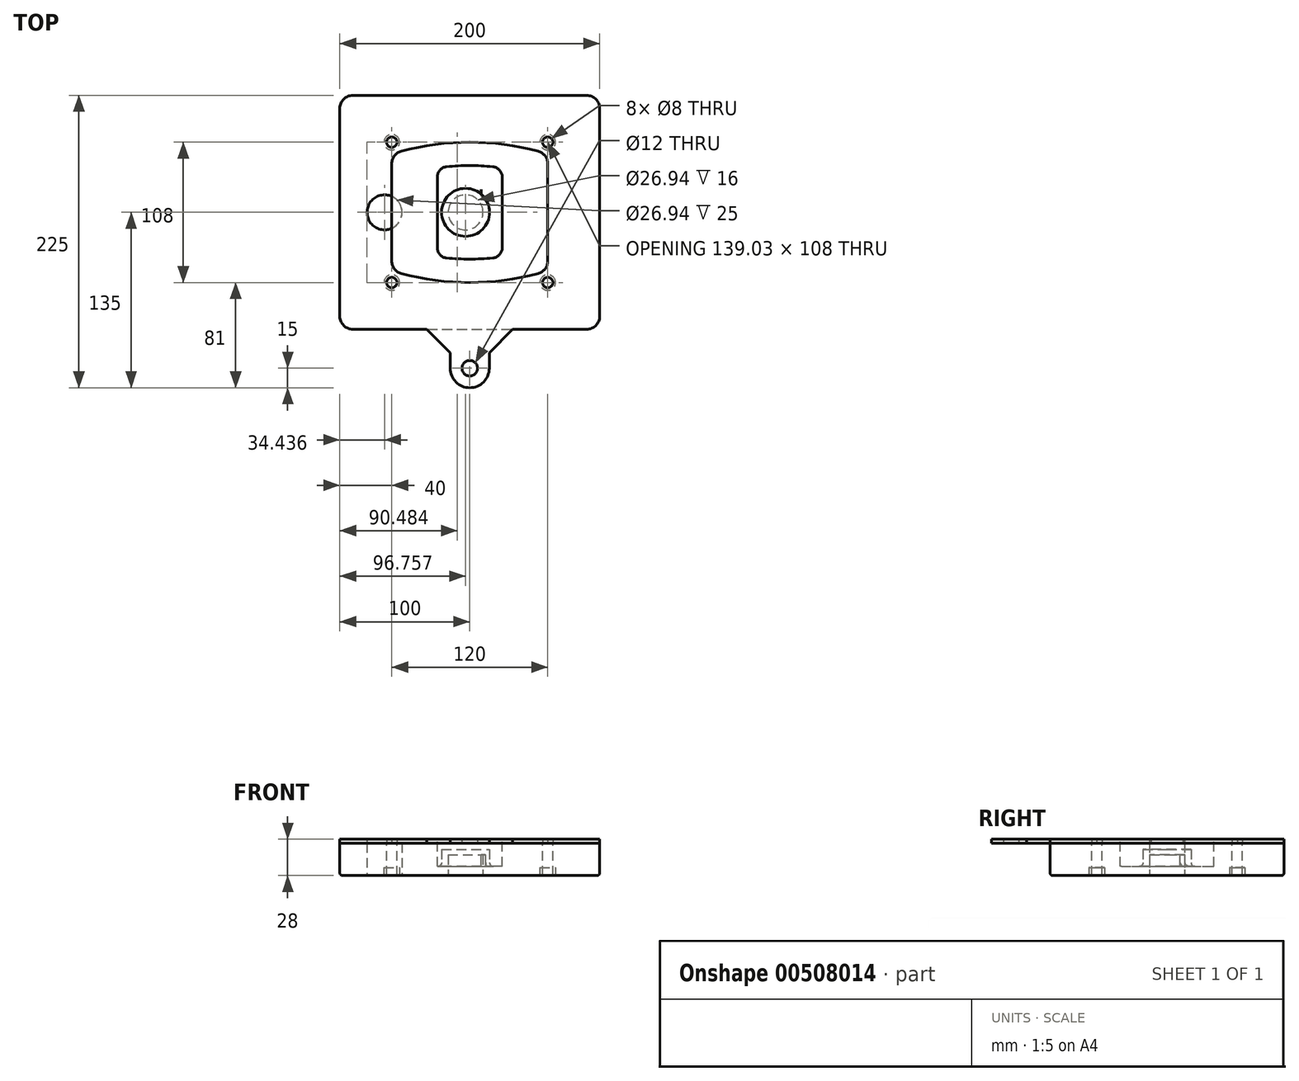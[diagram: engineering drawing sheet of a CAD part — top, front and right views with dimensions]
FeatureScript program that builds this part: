
annotation { "Feature Type Name" : "Feature", "Feature Type Description" : "" }
export const myFeature = defineFeature(function(context is Context, id is Id, definition is map)
    precondition{}
    {
        {
            var Q0;
            Q0=qCreatedBy(makeId("Top.planeOp"),FACE);
            var sketch = newSketch(context, id + "F0", { "sketchPlane" : qUnion([Q0])});
            skPoint(sketch, "E0.rect.middle", {"position": v(0, 0) * mm});
            skLineSegment(sketch, "E1.bottom", {"start": v(-90, -90) * mm, "end": v(90, -90) * mm});
            skLineSegment(sketch, "E1.top", {"start": v(-90, 90) * mm, "end": v(90, 90) * mm});
            skLineSegment(sketch, "E1.left", {"start": v(-100, -80) * mm, "end": v(-100, 80) * mm});
            skLineSegment(sketch, "E1.right", {"start": v(100, -80) * mm, "end": v(100, 80) * mm});
            skLineSegment(sketch, "E2", {"start": v(-100, 90) * mm, "end": v(100, -90) * mm, "construction": true});
            skLineSegment(sketch, "E3", {"start": v(100, 90) * mm, "end": v(-100, -90) * mm, "construction": true});
            skCircle(sketch, "E4", {"center": v(-60, 54) * mm, "radius": 4 * mm});
            skCircle(sketch, "E5", {"center": v(60, 54) * mm, "radius": 4 * mm});
            skCircle(sketch, "E6", {"center": v(60, -54) * mm, "radius": 4 * mm});
            skCircle(sketch, "E7", {"center": v(-60, -54) * mm, "radius": 4 * mm});
            skLineSegment(sketch, "E8", {"start": v(-60, 54) * mm, "end": v(60, 54) * mm, "construction": true});
            skLineSegment(sketch, "E9", {"start": v(60, 54) * mm, "end": v(60, -54) * mm, "construction": true});
            skLineSegment(sketch, "E10", {"start": v(60, -54) * mm, "end": v(-60, -54) * mm, "construction": true});
            skLineSegment(sketch, "E11", {"start": v(-60, -54) * mm, "end": v(-60, 54) * mm, "construction": true});
            skLineSegment(sketch, "E12", {"start": v(-60, 37.46) * mm, "end": v(-60, -37.46) * mm});
            skLineSegment(sketch, "E13", {"start": v(60, 37.46) * mm, "end": v(60, -37.46) * mm});
            skArc(sketch, "E14", {"start": v(52.57, 47.13) * mm, "mid": v(0, 54) * mm, "end": v(-52.57, 47.13) * mm});
            skArc(sketch, "E15", {"start": v(-52.57, -47.13) * mm, "mid": v(0, -54) * mm, "end": v(52.57, -47.13) * mm});
            skLineSegment(sketch, "E16", {"start": v(-60, 0) * mm, "end": v(60, 0) * mm, "construction": true});
            skPoint(sketch, "E17.visualSharp", {"position": v(-60, -45) * mm});
            skArc(sketch, "E17.filletArc", {"start": v(-60, -37.46) * mm, "mid": v(-57.93, -43.56) * mm, "end": v(-52.57, -47.13) * mm});
            skPoint(sketch, "E18.visualSharp", {"position": v(-60, 45) * mm});
            skArc(sketch, "E18.filletArc", {"start": v(-52.57, 47.13) * mm, "mid": v(-57.93, 43.56) * mm, "end": v(-60, 37.46) * mm});
            skPoint(sketch, "E19.visualSharp", {"position": v(60, 45) * mm});
            skArc(sketch, "E19.filletArc", {"start": v(60, 37.46) * mm, "mid": v(57.93, 43.56) * mm, "end": v(52.57, 47.13) * mm});
            skPoint(sketch, "E20.visualSharp", {"position": v(60, -45) * mm});
            skArc(sketch, "E20.filletArc", {"start": v(52.57, -47.13) * mm, "mid": v(57.93, -43.56) * mm, "end": v(60, -37.46) * mm});
            skPoint(sketch, "E21.visualSharp", {"position": v(-100, 90) * mm});
            skArc(sketch, "E21.filletArc", {"start": v(-90, 90) * mm, "mid": v(-97.07, 87.07) * mm, "end": v(-100, 80) * mm});
            skPoint(sketch, "E22.visualSharp", {"position": v(100, 90) * mm});
            skArc(sketch, "E22.filletArc", {"start": v(100, 80) * mm, "mid": v(97.07, 87.07) * mm, "end": v(90, 90) * mm});
            skPoint(sketch, "E23.visualSharp", {"position": v(100, -90) * mm});
            skArc(sketch, "E23.filletArc", {"start": v(90, -90) * mm, "mid": v(97.07, -87.07) * mm, "end": v(100, -80) * mm});
            skPoint(sketch, "E24.visualSharp", {"position": v(-100, -90) * mm});
            skArc(sketch, "E24.filletArc", {"start": v(-100, -80) * mm, "mid": v(-97.07, -87.07) * mm, "end": v(-90, -90) * mm});
            skArc(sketch, "E25.0", {"start": v(57, 37.46) * mm, "mid": v(55.55, 41.73) * mm, "end": v(51.8, 44.23) * mm});
            skLineSegment(sketch, "E25.1", {"start": v(57, 37.46) * mm, "end": v(57, -37.46) * mm});
            skArc(sketch, "E25.2", {"start": v(51.8, -44.23) * mm, "mid": v(55.55, -41.73) * mm, "end": v(57, -37.46) * mm});
            skArc(sketch, "E25.3", {"start": v(-51.8, -44.23) * mm, "mid": v(0, -51) * mm, "end": v(51.8, -44.23) * mm});
            skArc(sketch, "E25.4", {"start": v(-57, -37.46) * mm, "mid": v(-55.55, -41.73) * mm, "end": v(-51.8, -44.23) * mm});
            skArc(sketch, "E25.5", {"start": v(51.8, 44.23) * mm, "mid": v(0, 51) * mm, "end": v(-51.8, 44.23) * mm});
            skLineSegment(sketch, "E25.6", {"start": v(-57, 37.46) * mm, "end": v(-57, -37.46) * mm});
            skArc(sketch, "E25.7", {"start": v(-51.8, 44.23) * mm, "mid": v(-55.55, 41.73) * mm, "end": v(-57, 37.46) * mm});
            skArc(sketch, "E26.0", {"start": v(-53.6, 51) * mm, "mid": v(-61.1, 46) * mm, "end": v(-64, 37.46) * mm});
            skArc(sketch, "E26.1", {"start": v(53.6, 51) * mm, "mid": v(0, 58) * mm, "end": v(-53.6, 51) * mm});
            skArc(sketch, "E26.2", {"start": v(64, 37.46) * mm, "mid": v(61.1, 46) * mm, "end": v(53.6, 51) * mm});
            skLineSegment(sketch, "E26.3", {"start": v(64, 37.46) * mm, "end": v(64, -37.46) * mm});
            skArc(sketch, "E26.4", {"start": v(53.6, -51) * mm, "mid": v(61.1, -46) * mm, "end": v(64, -37.46) * mm});
            skLineSegment(sketch, "E26.5", {"start": v(-64, 37.46) * mm, "end": v(-64, -37.46) * mm});
            skArc(sketch, "E26.6", {"start": v(-53.6, -51) * mm, "mid": v(0, -58) * mm, "end": v(53.6, -51) * mm});
            skArc(sketch, "E26.7", {"start": v(-64, -37.46) * mm, "mid": v(-61.1, -46) * mm, "end": v(-53.6, -51) * mm});
            skSolve(sketch);
        }
        {
            var Q0;
            Q0=makeQuery(id+"F0.imprint","IMPRINT",FACE,{"disambiguationData":[TD([[makeQuery(id+"F0.imprint","IMPRINT",EDGE,{"derivedFrom":sQuery(id+"F0.wireOp",EDGE,"E1.bottom")}),1.0]])]});
            var Q1;
            Q1=makeQuery(id+"F0.imprint","IMPRINT",FACE,{"disambiguationData":[TD([[makeQuery(id+"F0.imprint","IMPRINT",EDGE,{"derivedFrom":sQuery(id+"F0.wireOp",EDGE,"E12")}),1.0]])]});
            var Q2;
            Q2=makeQuery(id+"F0.imprint","IMPRINT",FACE,{"disambiguationData":[TD([[makeQuery(id+"F0.imprint","IMPRINT",EDGE,{"derivedFrom":sQuery(id+"F0.wireOp",EDGE,"E25.0")}),1.0]])]});
            var Q3;
            Q3=makeQuery(id+"F0.imprint","IMPRINT",FACE,{"disambiguationData":[TD([[makeQuery(id+"F0.imprint","IMPRINT",EDGE,{"derivedFrom":sQuery(id+"F0.wireOp",EDGE,"E12")}),-1.0]])]});
            extrude(context, id + "F1", {"entities" : qUnion([Q0, Q1, Q2, Q3]), "oppositeDirection" : true, "depth" : 25 * mm});
        }
        {
            var Q0;
            Q0=makeQuery(id+"F0.imprint","IMPRINT",FACE,{"disambiguationData":[TD([[makeQuery(id+"F0.imprint","IMPRINT",EDGE,{"derivedFrom":sQuery(id+"F0.wireOp",EDGE,"E12")}),1.0]])]});
            extrude(context, id + "F2", {"entities" : qUnion([Q0]), "operationType" : NewBodyOperationType.ADD, "depth" : 3 * mm});
        }
        {
            var Q0;
            Q0=makeQuery(id+"F0.imprint","IMPRINT",FACE,{"disambiguationData":[TD([[makeQuery(id+"F0.imprint","IMPRINT",EDGE,{"derivedFrom":sQuery(id+"F0.wireOp",EDGE,"E25.0")}),1.0]])]});
            extrude(context, id + "F3", {"entities" : qUnion([Q0]), "operationType" : NewBodyOperationType.REMOVE, "oppositeDirection" : true, "depth" : 18 * mm});
        }
        {
            var Q0;
            Q0=makeQuery(id+"F2.opExtrude","CAP_FACE",FACE,{"disambiguationData":[OSD([sQuery(id+"F0.wireOp",EDGE,"E12"),sQuery(id+"F0.wireOp",EDGE,"E13"),sQuery(id+"F0.wireOp",EDGE,"E14"),sQuery(id+"F0.wireOp",EDGE,"E15"),sQuery(id+"F0.wireOp",EDGE,"E17.filletArc"),sQuery(id+"F0.wireOp",EDGE,"E18.filletArc"),sQuery(id+"F0.wireOp",EDGE,"E19.filletArc"),sQuery(id+"F0.wireOp",EDGE,"E20.filletArc"),sQuery(id+"F0.wireOp",EDGE,"E25.0"),sQuery(id+"F0.wireOp",EDGE,"E25.1"),sQuery(id+"F0.wireOp",EDGE,"E25.2"),sQuery(id+"F0.wireOp",EDGE,"E25.3"),sQuery(id+"F0.wireOp",EDGE,"E25.4"),sQuery(id+"F0.wireOp",EDGE,"E25.5"),sQuery(id+"F0.wireOp",EDGE,"E25.6"),sQuery(id+"F0.wireOp",EDGE,"E25.7")])],"isStart":false});
            var sketch = newSketch(context, id + "F4", { "sketchPlane" : qUnion([Q0])});
            skArc(sketch, "E27.0", {"start": v(-17.76, -35.15) * mm, "mid": v(0, -36) * mm, "end": v(17.76, -35.15) * mm});
            skArc(sketch, "E28.0", {"start": v(17.76, 35.15) * mm, "mid": v(0, 36) * mm, "end": v(-17.76, 35.15) * mm});
            skLineSegment(sketch, "E29", {"start": v(-25, 27.19) * mm, "end": v(-25, -27.19) * mm});
            skLineSegment(sketch, "E30", {"start": v(25, 27.19) * mm, "end": v(25, -27.19) * mm});
            skLineSegment(sketch, "E31", {"start": v(-25, 34.32) * mm, "end": v(25, 34.32) * mm, "construction": true});
            skLineSegment(sketch, "E32", {"start": v(-25, -34.32) * mm, "end": v(25, -34.32) * mm, "construction": true});
            skPoint(sketch, "E33.visualSharp", {"position": v(-25, 34.32) * mm});
            skArc(sketch, "E33.filletArc", {"start": v(-17.76, 35.15) * mm, "mid": v(-22.92, 32.57) * mm, "end": v(-25, 27.19) * mm});
            skPoint(sketch, "E34.visualSharp", {"position": v(25, 34.32) * mm});
            skArc(sketch, "E34.filletArc", {"start": v(25, 27.19) * mm, "mid": v(22.92, 32.57) * mm, "end": v(17.76, 35.15) * mm});
            skPoint(sketch, "E35.visualSharp", {"position": v(25, -34.32) * mm});
            skArc(sketch, "E35.filletArc", {"start": v(17.76, -35.15) * mm, "mid": v(22.92, -32.57) * mm, "end": v(25, -27.19) * mm});
            skPoint(sketch, "E36.visualSharp", {"position": v(-25, -34.32) * mm});
            skArc(sketch, "E36.filletArc", {"start": v(-25, -27.19) * mm, "mid": v(-22.92, -32.57) * mm, "end": v(-17.76, -35.15) * mm});
            skArc(sketch, "E37.0", {"start": v(51.8, 44.23) * mm, "mid": v(0, 51) * mm, "end": v(-51.8, 44.23) * mm});
            skArc(sketch, "E37.1", {"start": v(-51.8, 44.23) * mm, "mid": v(-55.55, 41.73) * mm, "end": v(-57, 37.46) * mm});
            skLineSegment(sketch, "E37.2", {"start": v(-57, 37.46) * mm, "end": v(-57, -37.46) * mm});
            skArc(sketch, "E37.3", {"start": v(-57, -37.46) * mm, "mid": v(-55.55, -41.73) * mm, "end": v(-51.8, -44.23) * mm});
            skArc(sketch, "E37.4", {"start": v(-51.8, -44.23) * mm, "mid": v(0, -51) * mm, "end": v(51.8, -44.23) * mm});
            skArc(sketch, "E37.5", {"start": v(51.8, -44.23) * mm, "mid": v(55.55, -41.73) * mm, "end": v(57, -37.46) * mm});
            skLineSegment(sketch, "E37.6", {"start": v(57, 37.46) * mm, "end": v(57, -37.46) * mm});
            skArc(sketch, "E37.7", {"start": v(57, 37.46) * mm, "mid": v(55.55, 41.73) * mm, "end": v(51.8, 44.23) * mm});
            skLineSegment(sketch, "E38.0", {"start": v(23, 27.19) * mm, "end": v(23, -27.19) * mm});
            skArc(sketch, "E38.1", {"start": v(17.57, -33.16) * mm, "mid": v(21.44, -31.22) * mm, "end": v(23, -27.19) * mm});
            skArc(sketch, "E38.2", {"start": v(-17.57, -33.16) * mm, "mid": v(0, -34) * mm, "end": v(17.57, -33.16) * mm});
            skArc(sketch, "E38.3", {"start": v(-23, -27.19) * mm, "mid": v(-21.44, -31.22) * mm, "end": v(-17.57, -33.16) * mm});
            skLineSegment(sketch, "E38.4", {"start": v(-23, 27.19) * mm, "end": v(-23, -27.19) * mm});
            skArc(sketch, "E38.5", {"start": v(23, 27.19) * mm, "mid": v(21.44, 31.22) * mm, "end": v(17.57, 33.16) * mm});
            skArc(sketch, "E38.6", {"start": v(-17.57, 33.16) * mm, "mid": v(-21.44, 31.22) * mm, "end": v(-23, 27.19) * mm});
            skArc(sketch, "E38.7", {"start": v(17.57, 33.16) * mm, "mid": v(0, 34) * mm, "end": v(-17.57, 33.16) * mm});
            skArc(sketch, "E39.0", {"start": v(21, 27.19) * mm, "mid": v(19.96, 29.88) * mm, "end": v(17.38, 31.17) * mm});
            skLineSegment(sketch, "E39.1", {"start": v(21, 27.19) * mm, "end": v(21, -27.19) * mm});
            skArc(sketch, "E39.2", {"start": v(17.38, -31.17) * mm, "mid": v(19.96, -29.88) * mm, "end": v(21, -27.19) * mm});
            skArc(sketch, "E39.3", {"start": v(-17.38, -31.17) * mm, "mid": v(0, -32) * mm, "end": v(17.38, -31.17) * mm});
            skArc(sketch, "E39.4", {"start": v(-21, -27.19) * mm, "mid": v(-19.96, -29.88) * mm, "end": v(-17.38, -31.17) * mm});
            skArc(sketch, "E39.5", {"start": v(17.38, 31.17) * mm, "mid": v(0, 32) * mm, "end": v(-17.38, 31.17) * mm});
            skLineSegment(sketch, "E39.6", {"start": v(-21, 27.19) * mm, "end": v(-21, -27.19) * mm});
            skArc(sketch, "E39.7", {"start": v(-17.38, 31.17) * mm, "mid": v(-19.96, 29.88) * mm, "end": v(-21, 27.19) * mm});
            skLineSegment(sketch, "E40", {"start": v(-25, 0) * mm, "end": v(25, 0) * mm, "construction": true});
            skLineSegment(sketch, "E41", {"start": v(-11, 5.5) * mm, "end": v(-11, 27.5) * mm});
            skLineSegment(sketch, "E42", {"start": v(-8, 30.5) * mm, "end": v(8, 30.5) * mm});
            skLineSegment(sketch, "E43", {"start": v(11, 27.5) * mm, "end": v(11, 13.5) * mm});
            skLineSegment(sketch, "E44", {"start": v(14, 10.5) * mm, "end": v(14, 10.5) * mm});
            skLineSegment(sketch, "E45", {"start": v(17, 7.5) * mm, "end": v(17, 5.5) * mm});
            skLineSegment(sketch, "E46", {"start": v(14, 2.5) * mm, "end": v(-8, 2.5) * mm});
            skPoint(sketch, "E47.visualSharp", {"position": v(-11, 30.5) * mm});
            skArc(sketch, "E47.filletArc", {"start": v(-8, 30.5) * mm, "mid": v(-10.12, 29.62) * mm, "end": v(-11, 27.5) * mm});
            skPoint(sketch, "E48.visualSharp", {"position": v(11, 30.5) * mm});
            skArc(sketch, "E48.filletArc", {"start": v(11, 27.5) * mm, "mid": v(10.12, 29.62) * mm, "end": v(8, 30.5) * mm});
            skPoint(sketch, "E49.visualSharp", {"position": v(11, 10.5) * mm});
            skArc(sketch, "E49.filletArc", {"start": v(11, 13.5) * mm, "mid": v(11.88, 11.38) * mm, "end": v(14, 10.5) * mm});
            skPoint(sketch, "E50.visualSharp", {"position": v(17, 10.5) * mm});
            skArc(sketch, "E50.filletArc", {"start": v(17, 7.5) * mm, "mid": v(16.12, 9.62) * mm, "end": v(14, 10.5) * mm});
            skPoint(sketch, "E51.visualSharp", {"position": v(17, 2.5) * mm});
            skArc(sketch, "E51.filletArc", {"start": v(14, 2.5) * mm, "mid": v(16.12, 3.38) * mm, "end": v(17, 5.5) * mm});
            skPoint(sketch, "E52.visualSharp", {"position": v(-11, 2.5) * mm});
            skArc(sketch, "E52.filletArc", {"start": v(-11, 5.5) * mm, "mid": v(-10.12, 3.38) * mm, "end": v(-8, 2.5) * mm});
            skLineSegment(sketch, "E53.0.MirrorCS", {"start": v(14, -2.5) * mm, "end": v(-8, -2.5) * mm});
            skArc(sketch, "E54.0.MirrorCS", {"start": v(-11, -5.5) * mm, "mid": v(-10.12, -3.38) * mm, "end": v(-8, -2.5) * mm});
            skLineSegment(sketch, "E55.0.MirrorCS", {"start": v(-11, -5.5) * mm, "end": v(-11, -27.5) * mm});
            skArc(sketch, "E56.0.MirrorCS", {"start": v(-8, -30.5) * mm, "mid": v(-10.12, -29.62) * mm, "end": v(-11, -27.5) * mm});
            skLineSegment(sketch, "E57.0.MirrorCS", {"start": v(-8, -30.5) * mm, "end": v(8, -30.5) * mm});
            skArc(sketch, "E58.0.MirrorCS", {"start": v(11, -27.5) * mm, "mid": v(10.12, -29.62) * mm, "end": v(8, -30.5) * mm});
            skLineSegment(sketch, "E59.0.MirrorCS", {"start": v(11, -27.5) * mm, "end": v(11, -13.5) * mm});
            skArc(sketch, "E60.0.MirrorCS", {"start": v(11, -13.5) * mm, "mid": v(11.88, -11.38) * mm, "end": v(14, -10.5) * mm});
            skArc(sketch, "E61.0.MirrorCS", {"start": v(17, -7.5) * mm, "mid": v(16.12, -9.62) * mm, "end": v(14, -10.5) * mm});
            skLineSegment(sketch, "E62.0.MirrorCS", {"start": v(17, -7.5) * mm, "end": v(17, -5.5) * mm});
            skArc(sketch, "E63.0.MirrorCS", {"start": v(14, -2.5) * mm, "mid": v(16.12, -3.38) * mm, "end": v(17, -5.5) * mm});
            skSolve(sketch);
        }
        {
            var Q0;
            Q0 = qSketchRegion(id + "F4", true);
            extrude(context, id + "F5", {"entities" : qUnion([Q0]), "operationType" : NewBodyOperationType.ADD, "endBound" : BoundingType.UP_TO_NEXT, "oppositeDirection" : true, "depth" : 25 * mm});
        }
        {
            var Q0;
            Q0=makeQuery(id+"F4.imprint","IMPRINT",FACE,{"disambiguationData":[TD([[makeQuery(id+"F4.imprint","IMPRINT",EDGE,{"derivedFrom":sQuery(id+"F4.wireOp",EDGE,"E38.0")}),-1.0]])]});
            extrude(context, id + "F6", {"entities" : qUnion([Q0]), "operationType" : NewBodyOperationType.REMOVE, "oppositeDirection" : true, "depth" : 2 * mm});
        }
        {
            var Q0;
            Q0=makeQuery(id+"F1.opExtrude","CAP_FACE",FACE,{"disambiguationData":[OSD([sQuery(id+"F0.wireOp",EDGE,"E1.bottom"),sQuery(id+"F0.wireOp",EDGE,"E1.top"),sQuery(id+"F0.wireOp",EDGE,"E1.left"),sQuery(id+"F0.wireOp",EDGE,"E1.right"),sQuery(id+"F0.wireOp",EDGE,"E4"),sQuery(id+"F0.wireOp",EDGE,"E5"),sQuery(id+"F0.wireOp",EDGE,"E6"),sQuery(id+"F0.wireOp",EDGE,"E7"),sQuery(id+"F0.wireOp",EDGE,"E21.filletArc"),sQuery(id+"F0.wireOp",EDGE,"E22.filletArc"),sQuery(id+"F0.wireOp",EDGE,"E23.filletArc"),sQuery(id+"F0.wireOp",EDGE,"E24.filletArc")])],"isStart":false});
            var sketch = newSketch(context, id + "F7", { "sketchPlane" : qUnion([Q0])});
            skCircle(sketch, "E64", {"center": v(-3.24, 0) * mm, "radius": 13.47 * mm});
            skCircle(sketch, "E65", {"center": v(-65.56, 0) * mm, "radius": 13.47 * mm});
            skLineSegment(sketch, "E66", {"start": v(100, 0) * mm, "end": v(-100, 0) * mm});
            skCircle(sketch, "E67", {"center": v(-3.24, 0) * mm, "radius": 18.47 * mm});
            skCircle(sketch, "E68", {"center": v(60, -54) * mm, "radius": 6 * mm});
            skCircle(sketch, "E69", {"center": v(-60, -54) * mm, "radius": 6 * mm});
            skCircle(sketch, "E70", {"center": v(-60, 54) * mm, "radius": 6 * mm});
            skCircle(sketch, "E71", {"center": v(60, 54) * mm, "radius": 6 * mm});
            skSolve(sketch);
        }
        {
            var Q0;
            {var subQ1=sQuery(id+"F7.wireOp",EDGE,"E66");var subQ4=sQuery(id+"F7.wireOp",EDGE,"E64");var subQ6=makeQuery(id+"F7.imprint","INTERSECT",VERTEX,{"disambiguationData":[OD(0.0)],"derivedFrom":[subQ4,subQ1]});Q0=makeQuery(id+"F7.imprint","IMPRINT",FACE,{"disambiguationData":[TD([[makeQuery(id+"F7.imprint","IMPRINT",EDGE,{"disambiguationData":[TD([[subQ6,-1.0]])],"derivedFrom":subQ4}),-1.0]])]});}
            var Q1;
            {var subQ0=sQuery(id+"F7.wireOp",EDGE,"E66");var subQ1=sQuery(id+"F7.wireOp",EDGE,"E64");var subQ3=makeQuery(id+"F7.imprint","INTERSECT",VERTEX,{"disambiguationData":[OD(0.0)],"derivedFrom":[subQ1,subQ0]});Q1=makeQuery(id+"F7.imprint","IMPRINT",FACE,{"disambiguationData":[TD([[makeQuery(id+"F7.imprint","IMPRINT",EDGE,{"disambiguationData":[TD([[subQ3,-1.0]])],"derivedFrom":subQ1}),1.0]])]});}
            var Q2;
            {var subQ0=sQuery(id+"F7.wireOp",EDGE,"E66");var subQ1=sQuery(id+"F7.wireOp",EDGE,"E64");var subQ3=makeQuery(id+"F7.imprint","INTERSECT",VERTEX,{"disambiguationData":[OD(0.0)],"derivedFrom":[subQ1,subQ0]});Q2=makeQuery(id+"F7.imprint","IMPRINT",FACE,{"disambiguationData":[TD([[makeQuery(id+"F7.imprint","IMPRINT",EDGE,{"disambiguationData":[TD([[subQ3,1.0]])],"derivedFrom":subQ1}),1.0]])]});}
            var Q3;
            {var subQ1=sQuery(id+"F7.wireOp",EDGE,"E66");var subQ4=sQuery(id+"F7.wireOp",EDGE,"E64");var subQ6=makeQuery(id+"F7.imprint","INTERSECT",VERTEX,{"disambiguationData":[OD(0.0)],"derivedFrom":[subQ4,subQ1]});Q3=makeQuery(id+"F7.imprint","IMPRINT",FACE,{"disambiguationData":[TD([[makeQuery(id+"F7.imprint","IMPRINT",EDGE,{"disambiguationData":[TD([[subQ6,1.0]])],"derivedFrom":subQ4}),-1.0]])]});}
            extrude(context, id + "F8", {"entities" : qUnion([Q0, Q1, Q2, Q3]), "operationType" : NewBodyOperationType.ADD, "oppositeDirection" : true, "depth" : 20 * mm});
        }
        {
            var Q0;
            {var subQ0=sQuery(id+"F7.wireOp",EDGE,"E66");var subQ1=sQuery(id+"F7.wireOp",EDGE,"E64");var subQ3=makeQuery(id+"F7.imprint","INTERSECT",VERTEX,{"disambiguationData":[OD(0.0)],"derivedFrom":[subQ1,subQ0]});Q0=makeQuery(id+"F7.imprint","IMPRINT",FACE,{"disambiguationData":[TD([[makeQuery(id+"F7.imprint","IMPRINT",EDGE,{"disambiguationData":[TD([[subQ3,-1.0]])],"derivedFrom":subQ1}),1.0]])]});}
            var Q1;
            {var subQ0=sQuery(id+"F7.wireOp",EDGE,"E66");var subQ1=sQuery(id+"F7.wireOp",EDGE,"E64");var subQ3=makeQuery(id+"F7.imprint","INTERSECT",VERTEX,{"disambiguationData":[OD(0.0)],"derivedFrom":[subQ1,subQ0]});Q1=makeQuery(id+"F7.imprint","IMPRINT",FACE,{"disambiguationData":[TD([[makeQuery(id+"F7.imprint","IMPRINT",EDGE,{"disambiguationData":[TD([[subQ3,1.0]])],"derivedFrom":subQ1}),1.0]])]});}
            var Q2;
            Q2 = qSketchRegion(id + "F93yIcf5vM4BNlw_1", true);
            var Q3;
            Q3 = qSketchRegion(id + "F4", true);
            extrude(context, id + "F9", {"entities" : qUnion([Q0, Q1, Q2, Q3]), "operationType" : NewBodyOperationType.REMOVE, "oppositeDirection" : true, "depth" : 16 * mm});
        }
        {
            var Q0;
            {var subQ0=sQuery(id+"F7.wireOp",EDGE,"E66");var subQ1=sQuery(id+"F7.wireOp",EDGE,"E65");var subQ3=makeQuery(id+"F7.imprint","INTERSECT",VERTEX,{"disambiguationData":[OD(0.0)],"derivedFrom":[subQ1,subQ0]});Q0=makeQuery(id+"F7.imprint","IMPRINT",FACE,{"disambiguationData":[TD([[makeQuery(id+"F7.imprint","IMPRINT",EDGE,{"disambiguationData":[TD([[subQ3,-1.0]])],"derivedFrom":subQ1}),1.0]])]});}
            var Q1;
            {var subQ0=sQuery(id+"F7.wireOp",EDGE,"E66");var subQ1=sQuery(id+"F7.wireOp",EDGE,"E65");var subQ3=makeQuery(id+"F7.imprint","INTERSECT",VERTEX,{"disambiguationData":[OD(0.0)],"derivedFrom":[subQ1,subQ0]});Q1=makeQuery(id+"F7.imprint","IMPRINT",FACE,{"disambiguationData":[TD([[makeQuery(id+"F7.imprint","IMPRINT",EDGE,{"disambiguationData":[TD([[subQ3,1.0]])],"derivedFrom":subQ1}),1.0]])]});}
            var Q2;
            Q2 = qSketchRegion(id + "F16", true);
            extrude(context, id + "F10", {"entities" : qUnion([Q0, Q1, Q2]), "operationType" : NewBodyOperationType.REMOVE, "oppositeDirection" : true, "depth" : 25 * mm});
        }
        {
            var Q0;
            Q0=makeQuery(id+"F7.imprint","IMPRINT",FACE,{"disambiguationData":[TD([[makeQuery(id+"F7.imprint","IMPRINT",EDGE,{"derivedFrom":sQuery(id+"F7.wireOp",EDGE,"E68")}),1.0]])]});
            var Q1;
            Q1=makeQuery(id+"F7.imprint","IMPRINT",FACE,{"disambiguationData":[TD([[makeQuery(id+"F7.imprint","IMPRINT",EDGE,{"derivedFrom":makeQuery(id+"F1.opExtrude","CAP_EDGE",EDGE,{"disambiguationData":[OSD([sQuery(id+"F0.wireOp",EDGE,"E5")])],"isStart":false})}),-1.0]])]});
            var Q2;
            Q2=makeQuery(id+"F7.imprint","IMPRINT",FACE,{"disambiguationData":[TD([[makeQuery(id+"F7.imprint","IMPRINT",EDGE,{"derivedFrom":sQuery(id+"F7.wireOp",EDGE,"E69")}),1.0]])]});
            var Q3;
            Q3=makeQuery(id+"F7.imprint","IMPRINT",FACE,{"disambiguationData":[TD([[makeQuery(id+"F7.imprint","IMPRINT",EDGE,{"derivedFrom":makeQuery(id+"F1.opExtrude","CAP_EDGE",EDGE,{"disambiguationData":[OSD([sQuery(id+"F0.wireOp",EDGE,"E4")])],"isStart":false})}),-1.0]])]});
            var Q4;
            Q4=makeQuery(id+"F7.imprint","IMPRINT",FACE,{"disambiguationData":[TD([[makeQuery(id+"F7.imprint","IMPRINT",EDGE,{"derivedFrom":sQuery(id+"F7.wireOp",EDGE,"E70")}),1.0]])]});
            var Q5;
            Q5=makeQuery(id+"F7.imprint","IMPRINT",FACE,{"disambiguationData":[TD([[makeQuery(id+"F7.imprint","IMPRINT",EDGE,{"derivedFrom":makeQuery(id+"F1.opExtrude","CAP_EDGE",EDGE,{"disambiguationData":[OSD([sQuery(id+"F0.wireOp",EDGE,"E7")])],"isStart":false})}),-1.0]])]});
            var Q6;
            Q6=makeQuery(id+"F7.imprint","IMPRINT",FACE,{"disambiguationData":[TD([[makeQuery(id+"F7.imprint","IMPRINT",EDGE,{"derivedFrom":sQuery(id+"F7.wireOp",EDGE,"E71")}),1.0]])]});
            var Q7;
            Q7=makeQuery(id+"F7.imprint","IMPRINT",FACE,{"disambiguationData":[TD([[makeQuery(id+"F7.imprint","IMPRINT",EDGE,{"derivedFrom":makeQuery(id+"F1.opExtrude","CAP_EDGE",EDGE,{"disambiguationData":[OSD([sQuery(id+"F0.wireOp",EDGE,"E6")])],"isStart":false})}),-1.0]])]});
            var Q8;
            Q8 = qSketchRegion(id + "F16", true);
            extrude(context, id + "F11", {"entities" : qUnion([Q0, Q1, Q2, Q3, Q4, Q5, Q6, Q7, Q8]), "oppositeDirection" : true, "depth" : 6 * mm});
        }
        {
            var Q0;
            Q0=makeQuery(id+"F9.boolean.opBoolean","COPY",FACE,{"derivedFrom":makeQuery(id+"F9.opExtrude","CAP_FACE",FACE,{"disambiguationData":[OSD([sQuery(id+"F7.wireOp",EDGE,"E64")])],"isStart":false})});
            var sketch = newSketch(context, id + "F12", { "sketchPlane" : qUnion([Q0])});
            skArc(sketch, "E72.0", {"start": v(10.76, -12.04) * mm, "mid": v(-16.64, 12.7) * mm, "end": v(9.52, -13.35) * mm});
            skArc(sketch, "E72.1", {"start": v(9.2, -13.65) * mm, "mid": v(-15.55, 13.77) * mm, "end": v(8.92, -13.9) * mm});
            skLineSegment(sketch, "E73", {"start": v(9.2, -13.65) * mm, "end": v(18.98, -13.65) * mm});
            skLineSegment(sketch, "E74.0", {"start": v(19.31, -13.35) * mm, "end": v(9.52, -13.35) * mm});
            skArc(sketch, "E74.1", {"start": v(19.31, -13.35) * mm, "mid": v(21.43, -12.47) * mm, "end": v(22.31, -10.35) * mm});
            skLineSegment(sketch, "E74.2", {"start": v(22.31, -8.35) * mm, "end": v(22.31, -10.35) * mm});
            skArc(sketch, "E74.3", {"start": v(22.31, -8.35) * mm, "mid": v(21.43, -6.23) * mm, "end": v(19.31, -5.35) * mm});
            skArc(sketch, "E74.4", {"start": v(10.76, -12.99) * mm, "mid": v(18.86, -13.44) * mm, "end": v(19.31, -5.35) * mm});
            skLineSegment(sketch, "E74.5", {"start": v(10.76, -12.04) * mm, "end": v(10.76, -12.99) * mm});
            skLineSegment(sketch, "E74.7", {"start": v(18.98, -13.65) * mm, "end": v(9.2, -13.65) * mm});
            skArc(sketch, "E74.8", {"start": v(18.98, -13.65) * mm, "mid": v(12.6, -11.33) * mm, "end": v(14.92, -4.95) * mm});
            skLineSegment(sketch, "E74.9", {"start": v(14.92, -6.95) * mm, "end": v(14.92, -4.95) * mm});
            skArc(sketch, "E74.10", {"start": v(14.92, -6.95) * mm, "mid": v(14.05, -9.07) * mm, "end": v(11.92, -9.95) * mm});
            skArc(sketch, "E74.11", {"start": v(8.92, -12.95) * mm, "mid": v(9.8, -10.83) * mm, "end": v(11.92, -9.95) * mm});
            skLineSegment(sketch, "E74.12", {"start": v(8.92, -13.9) * mm, "end": v(8.92, -12.95) * mm});
            skPoint(sketch, "E75.orphan", {"position": v(8.92, -26.95) * mm});
            skPoint(sketch, "E76.orphan", {"position": v(-3.02, -13.65) * mm});
            skPoint(sketch, "E77.orphan", {"position": v(-2.69, -13.35) * mm});
            skPoint(sketch, "E78.orphan", {"position": v(10.76, 1.01) * mm});
            skSolve(sketch);
        }
        {
            var Q0;
            {var subQ7=sQuery(id+"F12.wireOp",EDGE,"E72.0");var subQ14=sQuery(id+"F12.wireOp",EDGE,"E72.1");var subQ16=sQuery(id+"F12.wireOp",EDGE,"E74.1");var subQ18=sQuery(id+"F12.wireOp",EDGE,"E74.8");Q0=qUnion([makeQuery(id+"F12.imprint","IMPRINT",FACE,{"disambiguationData":[TD([[makeQuery(id+"F12.imprint","IMPRINT",EDGE,{"derivedFrom":subQ7}),1.0]])]}),makeQuery(id+"F12.imprint","IMPRINT",FACE,{"disambiguationData":[TD([[makeQuery(id+"F12.imprint","IMPRINT",EDGE,{"derivedFrom":subQ14}),1.0]])]}),makeQuery(id+"F12.imprint","IMPRINT",FACE,{"disambiguationData":[TD([[makeQuery(id+"F12.imprint","IMPRINT",EDGE,{"derivedFrom":subQ16}),1.0]])]}),makeQuery(id+"F12.imprint","IMPRINT",FACE,{"disambiguationData":[TD([[makeQuery(id+"F12.imprint","IMPRINT",EDGE,{"derivedFrom":subQ18}),-1.0]])]})]);}
            var Q1;
            Q1=makeQuery(id+"F3.boolean.opBoolean","COPY",FACE,{"derivedFrom":makeQuery(id+"F3.opExtrude","CAP_FACE",FACE,{"disambiguationData":[OSD([sQuery(id+"F0.wireOp",EDGE,"E25.0"),sQuery(id+"F0.wireOp",EDGE,"E25.1"),sQuery(id+"F0.wireOp",EDGE,"E25.2"),sQuery(id+"F0.wireOp",EDGE,"E25.3"),sQuery(id+"F0.wireOp",EDGE,"E25.4"),sQuery(id+"F0.wireOp",EDGE,"E25.5"),sQuery(id+"F0.wireOp",EDGE,"E25.6"),sQuery(id+"F0.wireOp",EDGE,"E25.7")])],"isStart":false})});
            extrude(context, id + "F13", {"entities" : qUnion([Q0]), "operationType" : NewBodyOperationType.REMOVE, "endBound" : BoundingType.UP_TO_SURFACE, "endBoundEntityFace" : qUnion([Q1]), "depth" : 25 * mm});
        }
        {
            var Q0;
            Q0=makeQuery(id+"F3.boolean.opBoolean","COPY",EDGE,{"derivedFrom":makeQuery(id+"F3.opExtrude","CAP_EDGE",EDGE,{"disambiguationData":[OSD([sQuery(id+"F0.wireOp",EDGE,"E25.6")])],"isStart":false})});
            var Q1;
            Q1=makeQuery(id+"F8.boolean.opBoolean","INTERSECT",EDGE,{"derivedFrom":[makeQuery(id+"F5.opExtrude","SWEPT_FACE",FACE,{"disambiguationData":[OSD([sQuery(id+"F4.wireOp",EDGE,"E30")])]}),makeQuery(id+"F8.opExtrude","CAP_FACE",FACE,{"disambiguationData":[OSD([sQuery(id+"F7.wireOp",EDGE,"E67")])],"isStart":false})]});
            var Q2;
            Q2=makeQuery(id+"F8.boolean.opBoolean","INTERSECT",EDGE,{"derivedFrom":[makeQuery(id+"F3.boolean.opBoolean","COPY",FACE,{"derivedFrom":makeQuery(id+"F3.opExtrude","CAP_FACE",FACE,{"disambiguationData":[OSD([sQuery(id+"F0.wireOp",EDGE,"E25.0"),sQuery(id+"F0.wireOp",EDGE,"E25.1"),sQuery(id+"F0.wireOp",EDGE,"E25.2"),sQuery(id+"F0.wireOp",EDGE,"E25.3"),sQuery(id+"F0.wireOp",EDGE,"E25.4"),sQuery(id+"F0.wireOp",EDGE,"E25.5"),sQuery(id+"F0.wireOp",EDGE,"E25.6"),sQuery(id+"F0.wireOp",EDGE,"E25.7")])],"isStart":false})}),makeQuery(id+"F8.opExtrude","SWEPT_FACE",FACE,{"disambiguationData":[OSD([sQuery(id+"F7.wireOp",EDGE,"E67")])]})]});
            var Q3;
            Q3=makeQuery(id+"F5.opExtrude","CAP_EDGE",EDGE,{"disambiguationData":[OSD([sQuery(id+"F4.wireOp",EDGE,"E30")])],"isStart":false});
            var Q4;
            Q4=makeQuery(id+"F8.boolean.opBoolean","INTERSECT",EDGE,{"derivedFrom":[makeQuery(id+"F3.boolean.opBoolean","COPY",FACE,{"derivedFrom":makeQuery(id+"F3.opExtrude","CAP_FACE",FACE,{"disambiguationData":[OSD([sQuery(id+"F0.wireOp",EDGE,"E25.0"),sQuery(id+"F0.wireOp",EDGE,"E25.1"),sQuery(id+"F0.wireOp",EDGE,"E25.2"),sQuery(id+"F0.wireOp",EDGE,"E25.3"),sQuery(id+"F0.wireOp",EDGE,"E25.4"),sQuery(id+"F0.wireOp",EDGE,"E25.5"),sQuery(id+"F0.wireOp",EDGE,"E25.6"),sQuery(id+"F0.wireOp",EDGE,"E25.7")])],"isStart":false})}),makeQuery(id+"F8.opExtrude","SWEPT_FACE",FACE,{"disambiguationData":[OSD([sQuery(id+"F7.wireOp",EDGE,"E67")])]})]});
            var Q5;
            Q5=makeQuery(id+"F8.boolean.opBoolean","INTERSECT",EDGE,{"derivedFrom":[makeQuery(id+"F3.boolean.opBoolean","COPY",FACE,{"derivedFrom":makeQuery(id+"F3.opExtrude","CAP_FACE",FACE,{"disambiguationData":[OSD([sQuery(id+"F0.wireOp",EDGE,"E25.0"),sQuery(id+"F0.wireOp",EDGE,"E25.1"),sQuery(id+"F0.wireOp",EDGE,"E25.2"),sQuery(id+"F0.wireOp",EDGE,"E25.3"),sQuery(id+"F0.wireOp",EDGE,"E25.4"),sQuery(id+"F0.wireOp",EDGE,"E25.5"),sQuery(id+"F0.wireOp",EDGE,"E25.6"),sQuery(id+"F0.wireOp",EDGE,"E25.7")])],"isStart":false})}),makeQuery(id+"F8.opExtrude","SWEPT_FACE",FACE,{"disambiguationData":[OSD([sQuery(id+"F7.wireOp",EDGE,"E67")])]})]});
            fillet(context, id + "F14", {"entities" : qUnion([Q0, Q1, Q2, Q3, Q4, Q5]), "radius" : 3 * mm, "tangentPropagation" : true, "allowEdgeOverflow" : false});
        }
        {
            var Q0;
            Q0=makeQuery(id+"F1.opExtrude","CAP_EDGE",EDGE,{"disambiguationData":[OSD([sQuery(id+"F0.wireOp",EDGE,"E1.bottom")])],"isStart":false});
            fillet(context, id + "F15", {"entities" : qUnion([Q0]), "radius" : 2 * mm, "tangentPropagation" : true, "allowEdgeOverflow" : false});
        }
        {
            var Q0;
            {var subQ0=sQuery(id+"F0.wireOp",EDGE,"E21.filletArc");var subQ1=sQuery(id+"F0.wireOp",EDGE,"E7");var subQ2=sQuery(id+"F0.wireOp",EDGE,"E6");var subQ3=sQuery(id+"F0.wireOp",EDGE,"E5");var subQ4=sQuery(id+"F0.wireOp",EDGE,"E4");var subQ5=sQuery(id+"F0.wireOp",EDGE,"E22.filletArc");var subQ6=sQuery(id+"F0.wireOp",EDGE,"E1.bottom");var subQ7=sQuery(id+"F0.wireOp",EDGE,"E1.right");var subQ8=sQuery(id+"F0.wireOp",EDGE,"E1.top");var subQ9=sQuery(id+"F0.wireOp",EDGE,"E1.left");var subQ10=sQuery(id+"F0.wireOp",EDGE,"E23.filletArc");var subQ11=sQuery(id+"F0.wireOp",EDGE,"E24.filletArc");Q0=makeQuery(id+"F2.boolean.opBoolean","SPLIT",FACE,{"disambiguationData":[TD([makeQuery(id+"F1.opExtrude","SWEPT_FACE",FACE,{"disambiguationData":[OSD([subQ6])]})])],"derivedFrom":makeQuery(id+"F1.opExtrude","CAP_FACE",FACE,{"disambiguationData":[OSD([subQ6,subQ8,subQ9,subQ7,subQ4,subQ3,subQ2,subQ1,subQ0,subQ5,subQ10,subQ11])],"isStart":true})});}
            var sketch = newSketch(context, id + "F16", { "sketchPlane" : qUnion([Q0])});
            skArc(sketch, "E79.0", {"start": v(100, 80) * mm, "mid": v(97.07, 87.07) * mm, "end": v(90, 90) * mm});
            skLineSegment(sketch, "E79.1", {"start": v(-90, 90) * mm, "end": v(90, 90) * mm});
            skCircle(sketch, "E79.2", {"center": v(60, 54) * mm, "radius": 4 * mm});
            skLineSegment(sketch, "E79.3", {"start": v(100, -80) * mm, "end": v(100, 80) * mm});
            skArc(sketch, "E79.4", {"start": v(52.57, 47.13) * mm, "mid": v(0, 54) * mm, "end": v(-52.57, 47.13) * mm});
            skArc(sketch, "E79.5", {"start": v(60, 37.46) * mm, "mid": v(57.93, 43.56) * mm, "end": v(52.57, 47.13) * mm});
            skLineSegment(sketch, "E79.6", {"start": v(60, 37.46) * mm, "end": v(60, -37.46) * mm});
            skLineSegment(sketch, "E79.7", {"start": v(-60, 37.46) * mm, "end": v(-60, -37.46) * mm});
            skCircle(sketch, "E79.8", {"center": v(-60, 54) * mm, "radius": 4 * mm});
            skArc(sketch, "E79.9", {"start": v(-52.57, 47.13) * mm, "mid": v(-57.93, 43.56) * mm, "end": v(-60, 37.46) * mm});
            skLineSegment(sketch, "E79.10", {"start": v(-100, -80) * mm, "end": v(-100, 80) * mm});
            skArc(sketch, "E79.11", {"start": v(-90, 90) * mm, "mid": v(-97.07, 87.07) * mm, "end": v(-100, 80) * mm});
            skArc(sketch, "E79.12", {"start": v(-60, -37.46) * mm, "mid": v(-57.93, -43.56) * mm, "end": v(-52.57, -47.13) * mm});
            skArc(sketch, "E79.13", {"start": v(-52.57, -47.13) * mm, "mid": v(0, -54) * mm, "end": v(52.57, -47.13) * mm});
            skArc(sketch, "E79.14", {"start": v(52.57, -47.13) * mm, "mid": v(57.93, -43.56) * mm, "end": v(60, -37.46) * mm});
            skArc(sketch, "E79.15", {"start": v(90, -90) * mm, "mid": v(97.07, -87.07) * mm, "end": v(100, -80) * mm});
            skCircle(sketch, "E79.16", {"center": v(60, -54) * mm, "radius": 4 * mm});
            skLineSegment(sketch, "E79.17", {"start": v(-90, -90) * mm, "end": v(90, -90) * mm});
            skArc(sketch, "E79.18", {"start": v(-100, -80) * mm, "mid": v(-97.07, -87.07) * mm, "end": v(-90, -90) * mm});
            skCircle(sketch, "E79.19", {"center": v(-60, -54) * mm, "radius": 4 * mm});
            skLineSegment(sketch, "E80", {"start": v(-33, 90) * mm, "end": v(-15, 108) * mm});
            skLineSegment(sketch, "E81", {"start": v(-15, 108) * mm, "end": v(-15, 120) * mm});
            skLineSegment(sketch, "E82", {"start": v(15, 108) * mm, "end": v(33, 90) * mm});
            skLineSegment(sketch, "E83", {"start": v(15, 108) * mm, "end": v(15, 120) * mm});
            skArc(sketch, "E84", {"start": v(15, 120) * mm, "mid": v(0, 135) * mm, "end": v(-15, 120) * mm});
            skCircle(sketch, "E85", {"center": v(0, 120) * mm, "radius": 6 * mm});
            skLineSegment(sketch, "E86", {"start": v(0, 120) * mm, "end": v(0, 90) * mm, "construction": true});
            skLineSegment(sketch, "E87.MirrorCS", {"start": v(33, 90) * mm, "end": v(15, 108) * mm});
            skArc(sketch, "E88.MirrorCS", {"start": v(-15, 120) * mm, "mid": v(0, 135) * mm, "end": v(15, 120) * mm});
            skLineSegment(sketch, "E89.MirrorCS", {"start": v(-15, 108) * mm, "end": v(-33, 90) * mm});
            skArc(sketch, "E90.MirrorCS", {"start": v(-15, -300) * mm, "mid": v(0, -315) * mm, "end": v(15, -300) * mm});
            skArc(sketch, "E91.MirrorCS", {"start": v(15, -300) * mm, "mid": v(0, -315) * mm, "end": v(-15, -300) * mm});
            skLineSegment(sketch, "E92.MirrorCS", {"start": v(15, -288) * mm, "end": v(15, -300) * mm});
            skCircle(sketch, "E93.MirrorC", {"center": v(0, -300) * mm, "radius": 6 * mm});
            skLineSegment(sketch, "E94.MirrorCS", {"start": v(-15, -288) * mm, "end": v(-15, -300) * mm});
            skLineSegment(sketch, "E95.MirrorCS", {"start": v(32.75, -270) * mm, "end": v(15, -288) * mm});
            skLineSegment(sketch, "E96.MirrorCS", {"start": v(-15, -288) * mm, "end": v(-33, -270) * mm});
            skLineSegment(sketch, "E97", {"start": v(-100, 0) * mm, "end": v(100, 0) * mm, "construction": true});
            skLineSegment(sketch, "E98.MirrorCS", {"start": v(-33, -90) * mm, "end": v(-15, -108) * mm});
            skLineSegment(sketch, "E99.MirrorCS", {"start": v(-15, -108) * mm, "end": v(-15, -120) * mm});
            skArc(sketch, "E100.MirrorCS", {"start": v(-15, -120) * mm, "mid": v(0, -135) * mm, "end": v(15, -120) * mm});
            skCircle(sketch, "E101.MirrorC", {"center": v(0, -120) * mm, "radius": 6 * mm});
            skLineSegment(sketch, "E102.MirrorCS", {"start": v(0, -120) * mm, "end": v(0, -90) * mm, "construction": true});
            skLineSegment(sketch, "E103.MirrorCS", {"start": v(15, -108) * mm, "end": v(15, -120) * mm});
            skLineSegment(sketch, "E104.MirrorCS", {"start": v(15, -108) * mm, "end": v(33, -90) * mm});
            skSolve(sketch);
        }
        {
            var Q0;
            {var subQ0=sQuery(id+"F16.wireOp",EDGE,"E87.MirrorCS");Q0=makeQuery(id+"F16.imprint","IMPRINT",FACE,{"disambiguationData":[TD([[makeQuery(id+"F16.imprint","IMPRINT",EDGE,{"derivedFrom":subQ0}),1.0]])]});}
            var Q1;
            {var subQ12=sQuery(id+"F16.wireOp",EDGE,"E79.0");Q1=makeQuery(id+"F16.imprint","IMPRINT",FACE,{"disambiguationData":[TD([[makeQuery(id+"F16.imprint","IMPRINT",EDGE,{"derivedFrom":subQ12}),1.0]])]});}
            var Q2;
            {var subQ0=sQuery(id+"F16.wireOp",EDGE,"E98.MirrorCS");Q2=makeQuery(id+"F16.imprint","IMPRINT",FACE,{"disambiguationData":[TD([[makeQuery(id+"F16.imprint","IMPRINT",EDGE,{"derivedFrom":subQ0}),1.0]])]});}
            var Q3;
            Q3=makeQuery(id+"F5.boolean.opBoolean","MERGE",FACE,{"derivedFrom":[makeQuery(id+"F2.opExtrude","CAP_FACE",FACE,{"disambiguationData":[OSD([sQuery(id+"F0.wireOp",EDGE,"E12"),sQuery(id+"F0.wireOp",EDGE,"E13"),sQuery(id+"F0.wireOp",EDGE,"E14"),sQuery(id+"F0.wireOp",EDGE,"E15"),sQuery(id+"F0.wireOp",EDGE,"E17.filletArc"),sQuery(id+"F0.wireOp",EDGE,"E18.filletArc"),sQuery(id+"F0.wireOp",EDGE,"E19.filletArc"),sQuery(id+"F0.wireOp",EDGE,"E20.filletArc"),sQuery(id+"F0.wireOp",EDGE,"E25.0"),sQuery(id+"F0.wireOp",EDGE,"E25.1"),sQuery(id+"F0.wireOp",EDGE,"E25.2"),sQuery(id+"F0.wireOp",EDGE,"E25.3"),sQuery(id+"F0.wireOp",EDGE,"E25.4"),sQuery(id+"F0.wireOp",EDGE,"E25.5"),sQuery(id+"F0.wireOp",EDGE,"E25.6"),sQuery(id+"F0.wireOp",EDGE,"E25.7")])],"isStart":false}),makeQuery(id+"F5.opExtrude","CAP_FACE",FACE,{"disambiguationData":[OSD([sQuery(id+"F4.wireOp",EDGE,"E27.0"),sQuery(id+"F4.wireOp",EDGE,"E28.0"),sQuery(id+"F4.wireOp",EDGE,"E29"),sQuery(id+"F4.wireOp",EDGE,"E30"),sQuery(id+"F4.wireOp",EDGE,"E33.filletArc"),sQuery(id+"F4.wireOp",EDGE,"E34.filletArc"),sQuery(id+"F4.wireOp",EDGE,"E35.filletArc"),sQuery(id+"F4.wireOp",EDGE,"E36.filletArc"),sQuery(id+"F4.wireOp",EDGE,"E37.0"),sQuery(id+"F4.wireOp",EDGE,"E37.1"),sQuery(id+"F4.wireOp",EDGE,"E37.2"),sQuery(id+"F4.wireOp",EDGE,"E37.3"),sQuery(id+"F4.wireOp",EDGE,"E37.4"),sQuery(id+"F4.wireOp",EDGE,"E37.5"),sQuery(id+"F4.wireOp",EDGE,"E37.6"),sQuery(id+"F4.wireOp",EDGE,"E37.7")])],"isStart":true})]});
            extrude(context, id + "F17", {"entities" : qUnion([Q0, Q1, Q2]), "endBound" : BoundingType.UP_TO_SURFACE, "endBoundEntityFace" : qUnion([Q3]), "depth" : 25 * mm, "offsetDistance" : 25 * mm});
        }
    });
